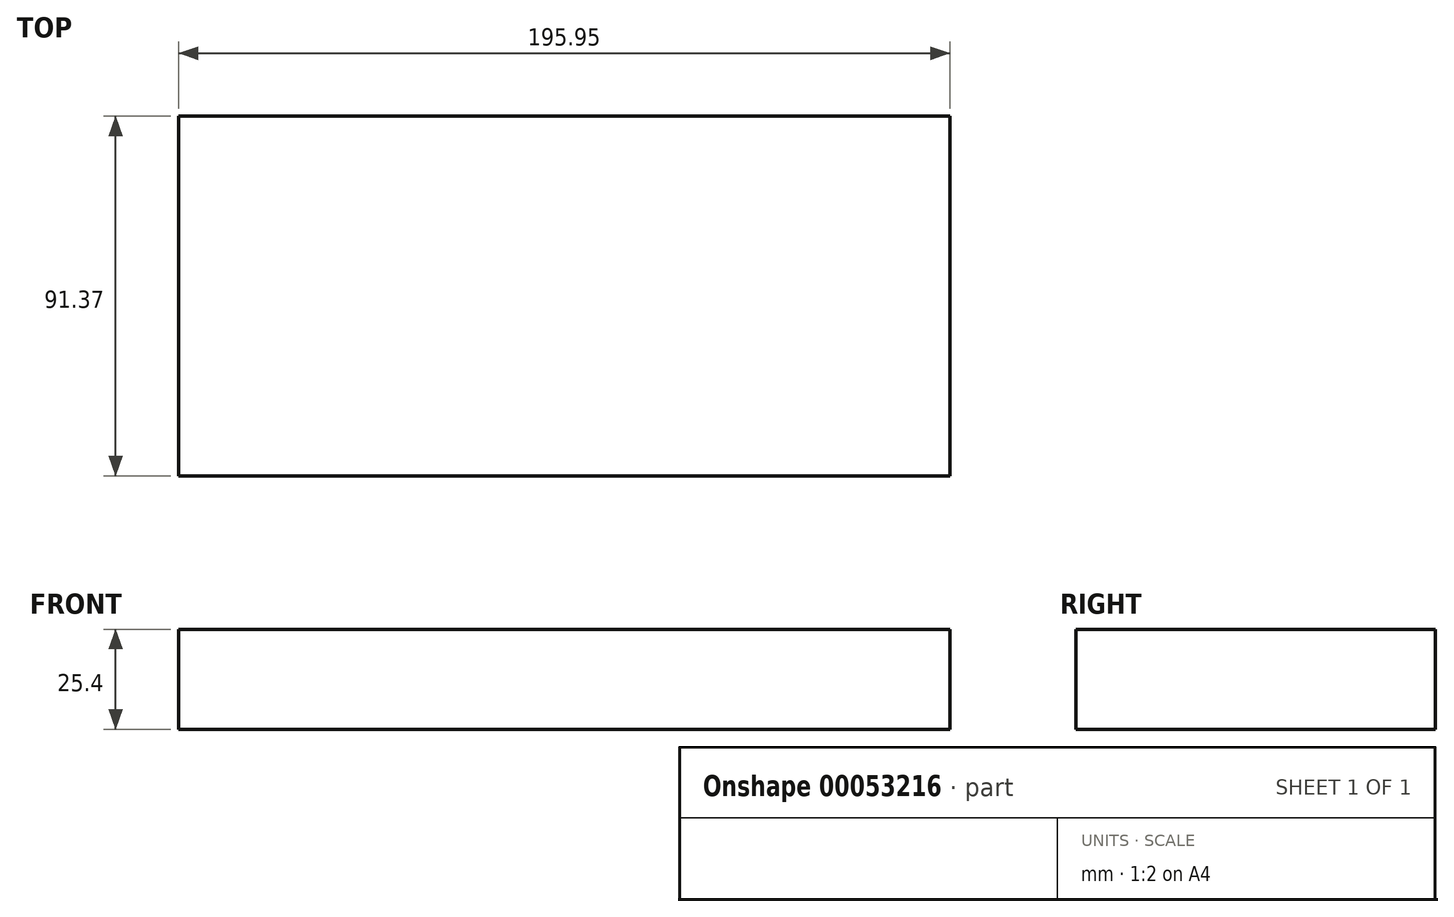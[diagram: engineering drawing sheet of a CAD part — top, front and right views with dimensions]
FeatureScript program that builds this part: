
annotation { "Feature Type Name" : "Feature", "Feature Type Description" : "" }
export const myFeature = defineFeature(function(context is Context, id is Id, definition is map)
    precondition{}
    {
        {
            var Q0;
            Q0=qCreatedBy(makeId("Top.planeOp"),FACE);
            var sketch = newSketch(context, id + "F0", { "sketchPlane" : qUnion([Q0])});
            skLineSegment(sketch, "E0", {"start": v(0, 0) * mm, "end": v(-195.95, 0) * mm});
            skLineSegment(sketch, "E1", {"start": v(-195.95, 0) * mm, "end": v(-195.95, 91.37) * mm});
            skLineSegment(sketch, "E2", {"start": v(-195.95, 91.37) * mm, "end": v(0, 91.37) * mm});
            skLineSegment(sketch, "E3", {"start": v(0, 91.37) * mm, "end": v(0, 0) * mm});
            skSolve(sketch);
        }
        {
            var Q0;
            Q0 = qSketchRegion(id + "F0", true);
            extrude(context, id + "F1", {"entities" : qUnion([Q0]), "depth" : 25.4 * mm});
        }
    });
